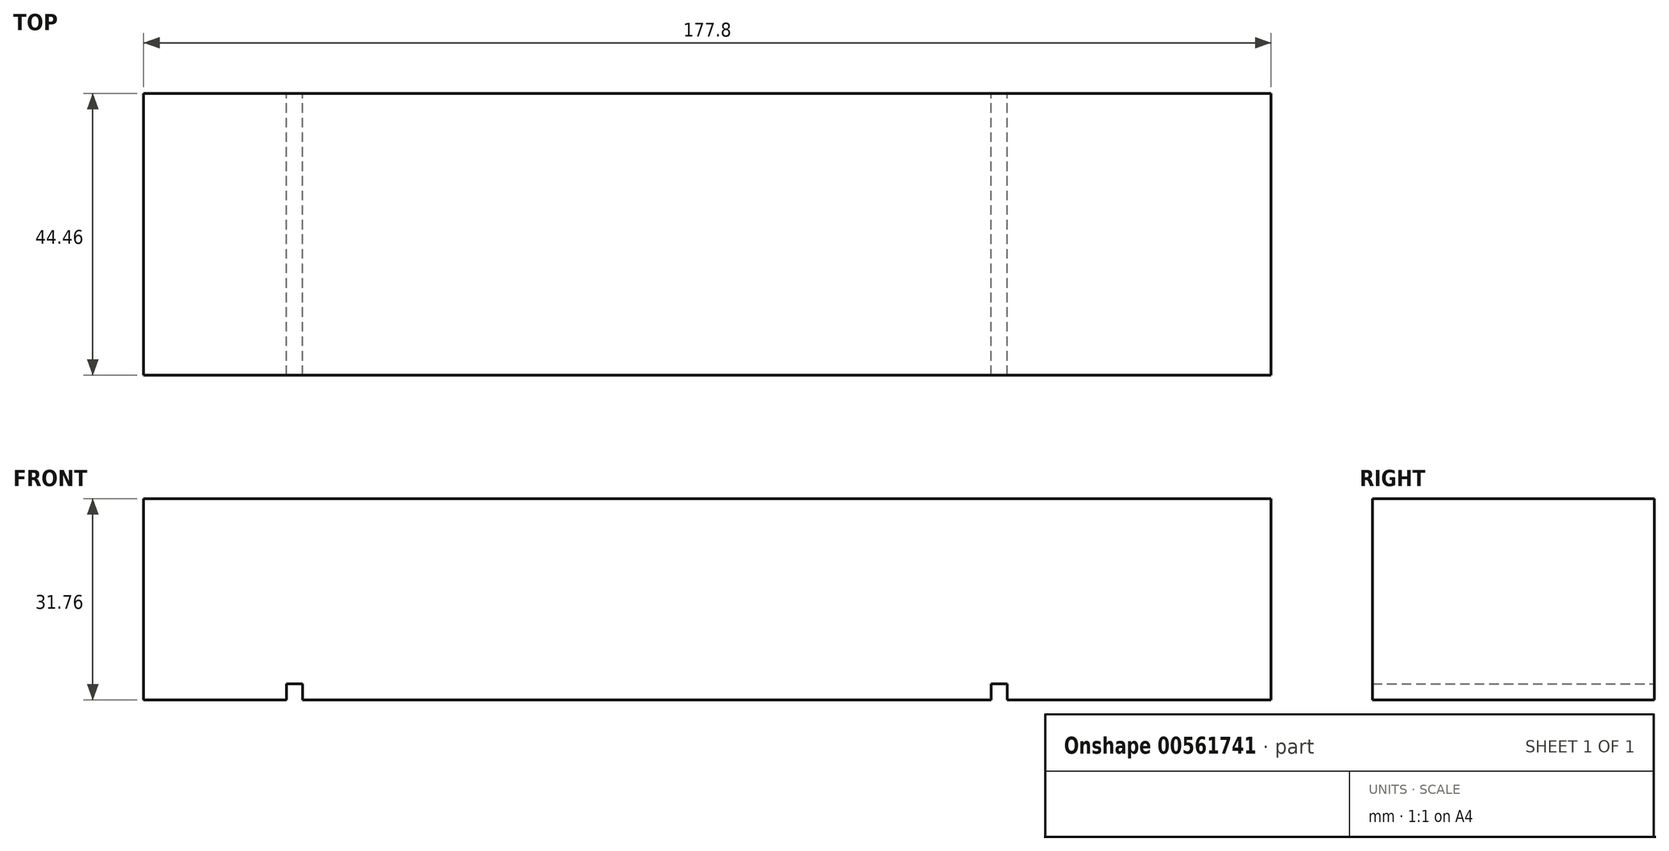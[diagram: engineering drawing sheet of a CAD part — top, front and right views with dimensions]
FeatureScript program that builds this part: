
annotation { "Feature Type Name" : "Feature", "Feature Type Description" : "" }
export const myFeature = defineFeature(function(context is Context, id is Id, definition is map)
    precondition{}
    {
        {
            var Q0;
            Q0=qCreatedBy(makeId("Front.planeOp"),FACE);
            var sketch = newSketch(context, id + "F0", { "sketchPlane" : qUnion([Q0])});
            skLineSegment(sketch, "E0.bottom", {"start": v(-88.9, -15.88) * mm, "end": v(88.9, -15.88) * mm});
            skLineSegment(sketch, "E0.top", {"start": v(-88.9, 15.88) * mm, "end": v(88.9, 15.88) * mm});
            skLineSegment(sketch, "E0.left", {"start": v(-88.9, -15.88) * mm, "end": v(-88.9, 15.88) * mm});
            skLineSegment(sketch, "E0.right", {"start": v(88.9, -15.88) * mm, "end": v(88.9, 15.88) * mm});
            skLineSegment(sketch, "E1", {"start": v(-88.9, 15.88) * mm, "end": v(88.9, -15.88) * mm, "construction": true});
            skPoint(sketch, "E2", {"position": v(0, 0) * mm});
            skSolve(sketch);
        }
        {
            var Q0;
            Q0=makeQuery(id+"F0.imprint","IMPRINT",FACE,{"disambiguationData":[TD([[makeQuery(id+"F0.imprint","IMPRINT",EDGE,{"derivedFrom":sQuery(id+"F0.wireOp",EDGE,"E0.bottom")}),1.0]])]});
            extrude(context, id + "F3", {"entities" : qUnion([Q0]), "endBound" : BoundingType.SYMMETRIC, "depth" : 44.45 * mm});
        }
        {
            var Q0;
            Q0=qCreatedBy(makeId("Front.planeOp"),FACE);
            var sketch = newSketch(context, id + "F1", { "sketchPlane" : qUnion([Q0])});
            skLineSegment(sketch, "E3.0", {"start": v(-88.9, -15.88) * mm, "end": v(88.9, -15.88) * mm, "construction": true});
            skLineSegment(sketch, "E4.bottom", {"start": v(-66.36, -15.88) * mm, "end": v(-63.82, -15.88) * mm});
            skLineSegment(sketch, "E4.top", {"start": v(-66.36, -13.34) * mm, "end": v(-63.82, -13.34) * mm});
            skLineSegment(sketch, "E4.left", {"start": v(-66.36, -15.88) * mm, "end": v(-66.36, -13.34) * mm});
            skLineSegment(sketch, "E4.right", {"start": v(-63.82, -15.88) * mm, "end": v(-63.82, -13.34) * mm});
            skLineSegment(sketch, "E5.bottom", {"start": v(44.77, -15.88) * mm, "end": v(47.3, -15.88) * mm});
            skLineSegment(sketch, "E5.top", {"start": v(44.77, -13.34) * mm, "end": v(47.3, -13.34) * mm});
            skLineSegment(sketch, "E5.left", {"start": v(44.77, -15.88) * mm, "end": v(44.77, -13.34) * mm});
            skLineSegment(sketch, "E5.right", {"start": v(47.3, -15.88) * mm, "end": v(47.3, -13.34) * mm});
            skPoint(sketch, "E6", {"position": v(-65.09, -15.88) * mm});
            skPoint(sketch, "E7", {"position": v(46.04, -15.88) * mm});
            skSolve(sketch);
        }
        {
            var Q0;
            Q0=qSketchRegion(id+"F1",true);
            extrude(context, id + "F2", {"entities" : qUnion([Q0]), "operationType" : NewBodyOperationType.REMOVE, "endBound" : BoundingType.UP_TO_NEXT, "depth" : 50.8 * mm, "hasSecondDirection" : true, "secondDirectionBound" : SecondDirectionBoundingType.UP_TO_NEXT, "secondDirectionOppositeDirection" : true, "secondDirectionDepth" : 25.4 * mm});
        }
    });
